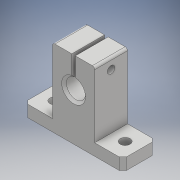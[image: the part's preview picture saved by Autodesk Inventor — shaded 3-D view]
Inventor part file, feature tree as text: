
AUTODESK INVENTOR PART (.ipt)
format: ipt  version: 2018 (Build 220112000, 112)  size: 182,784 bytes
history: native  units: mm
features: extrude x5, sketch x5, chamfer x2, fillet x1
ambient origin geometry x8: Origin, YZ Plane, XZ Plane, XY Plane, X Axis, Y Axis, Z Axis, Center Point
bodies: Solid1 (feature_tree)
feature tree (13):
  extrude  "Extrusion1"  Depth=33.0mm
  extrude  "Extrusion2"  Depth=9.0mm
  extrude  "Extrusion3"  Depth=8.15mm
  extrude  "Extrusion4"  Depth=1.5mm
  extrude  "Extrusion5"  Depth=10.0mm
  chamfer  "Chamfer2"  Distance=4.5mm
  fillet  "Fillet1"  Radius=10.0mm
  chamfer  "Chamfer3"  Distance=5.7mm
  sketch  "Sketch1"  dims[d0=5.0mm d1=33.0mm]
  sketch  "Sketch2"  dims[d2=21.0mm d3=9.0mm]
  sketch  "Sketch3"  dims[d4=14.0mm d5=0.0mm d6=8.15mm]
  sketch  "Sketch4"  dims[d7=13.0mm d8=1.5mm]
  sketch  "Sketch5"  dims[d9=10.0mm d10=0.0mm d11=3.2mm d13=4.5mm d14=10.0mm d15=0.0mm d16=5.7mm d17=6.5mm d18=2.6mm d19=0.0mm d20=4.2mm d22=2.6mm d23=0.0mm d27=1.5mm d28=2.0mm d29=45.0deg d30=1.0mm d31=1.0mm d32=2.0mm d33=45.0deg]
